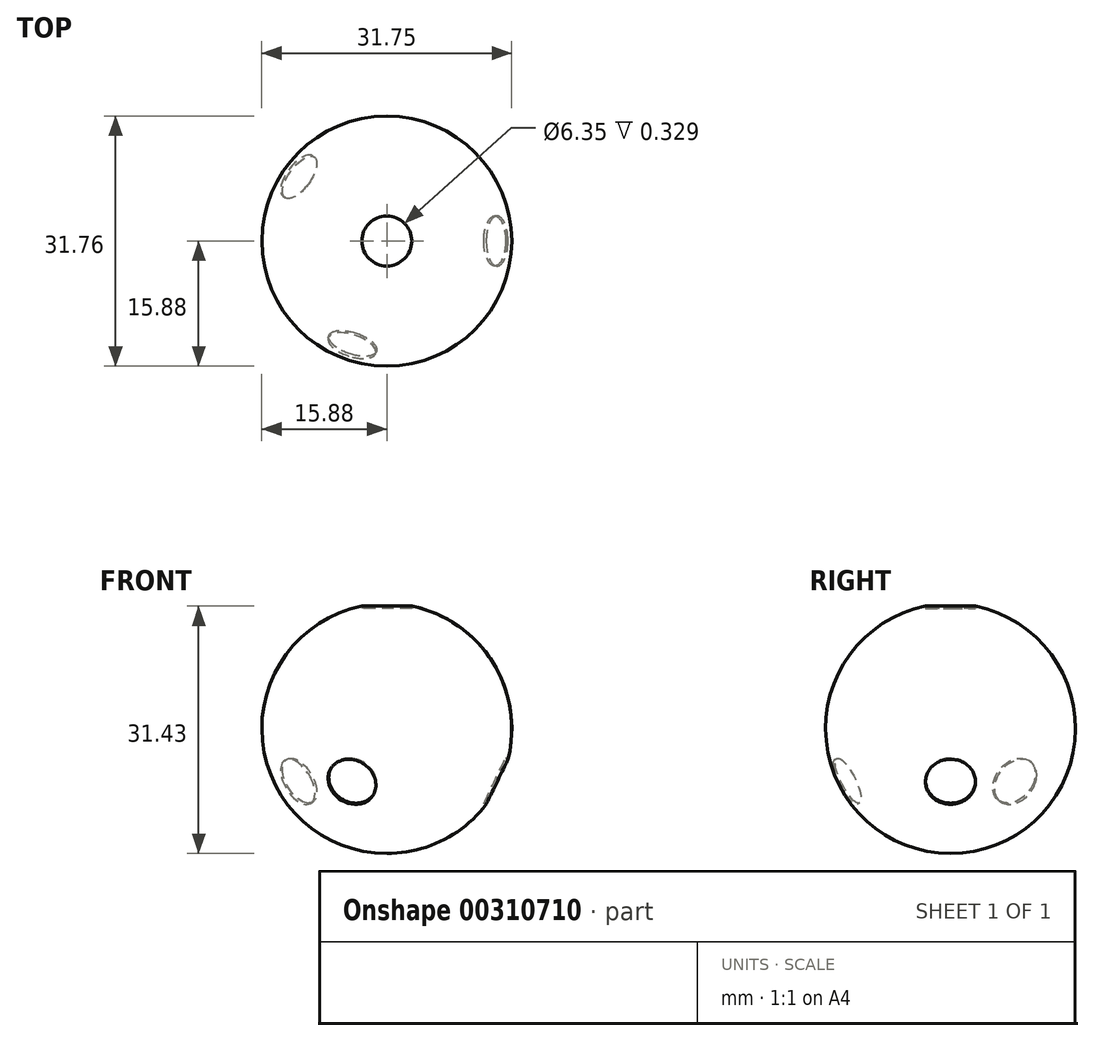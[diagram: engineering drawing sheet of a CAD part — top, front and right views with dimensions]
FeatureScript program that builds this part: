
annotation { "Feature Type Name" : "Feature", "Feature Type Description" : "" }
export const myFeature = defineFeature(function(context is Context, id is Id, definition is map)
    precondition{}
    {
        {
            var Q0;
            Q0=qCreatedBy(makeId("Front.planeOp"),FACE);
            var sketch = newSketch(context, id + "F0", { "sketchPlane" : qUnion([Q0])});
            skArc(sketch, "E0", {"start": v(0, 15.88) * mm, "mid": v(-15.88, 0) * mm, "end": v(0, -15.88) * mm});
            skLineSegment(sketch, "E1", {"start": v(0, 15.88) * mm, "end": v(0, -15.88) * mm});
            skSolve(sketch);
        }
        {
            var Q0;
            Q0=qCreatedBy(makeId("Top.planeOp"),FACE);
            var sketch = newSketch(context, id + "F1", { "sketchPlane" : qUnion([Q0])});
            skCircle(sketch, "E2", {"center": v(0, 0) * mm, "radius": 15.88 * mm});
            skSolve(sketch);
        }
        {
            var Q0;
            Q0=makeQuery(id+"F0.imprint","IMPRINT",FACE,{"disambiguationData":[TD([[makeQuery(id+"F0.imprint","IMPRINT",EDGE,{"derivedFrom":sQuery(id+"F0.wireOp",EDGE,"E0")}),1.0]])]});
            var Q1;
            Q1=sQuery(id+"F1.wireOp",EDGE,"E2");
            revolve(context, id + "F2", {"entities" : qUnion([Q0]), "axis" : qUnion([Q1]), "revolveType" : RevolveType.FULL});
        }
        {
            var Q0;
            Q0=qCreatedBy(makeId("Top.planeOp"),FACE);
            cPlane(context, id + "F3", {"entities" : qUnion([Q0]), "cplaneType" : CPlaneType.OFFSET, "offset" : 15.24 * mm, "width" : 152.4 * mm, "height" : 152.4 * mm});
        }
        {
            var Q0;
            Q0=qCreatedBy(id+"F3.planeOp",FACE);
            cPlane(context, id + "F4", {"entities" : qUnion([Q0]), "cplaneType" : CPlaneType.OFFSET, "offset" : 3 / 203.2 * mm, "oppositeDirection" : true, "width" : 152.4 * mm, "height" : 152.4 * mm});
        }
        {
            var Q0;
            Q0=qCreatedBy(id+"F4.planeOp",FACE);
            var sketch = newSketch(context, id + "F5", { "sketchPlane" : qUnion([Q0])});
            skCircle(sketch, "E3", {"center": v(0, 0) * mm, "radius": 3.18 * mm});
            skSolve(sketch);
        }
        {
            var Q0;
            Q0 = qSketchRegion(id + "F5", true);
            extrude(context, id + "F6", {"entities" : qUnion([Q0]), "depth" : 50.8 * mm});
        }
        {
            var Q0;
            Q0=qCreatedBy(makeId("Front.planeOp"),FACE);
            var sketch = newSketch(context, id + "F7", { "sketchPlane" : qUnion([Q0])});
            skLineSegment(sketch, "E4", {"start": v(0, 0) * mm, "end": v(0, -56.18) * mm, "construction": true});
            skLineSegment(sketch, "E5", {"start": v(0, 0) * mm, "end": v(-70.74, 0) * mm, "construction": true});
            skSolve(sketch);
        }
        {
            var Q0;
            Q0=qCreatedBy(makeId("Right.planeOp"),FACE);
            var sketch = newSketch(context, id + "F8", { "sketchPlane" : qUnion([Q0])});
            skLineSegment(sketch, "E6", {"start": v(0, 0) * mm, "end": v(67.72, 0) * mm, "construction": true});
            skSolve(sketch);
        }
        {
            var Q0;
            Q0=makeQuery(id+"F6.opExtrude","SWEPT_BODY",BODY,{"disambiguationData":[OSD([sQuery(id+"F5.wireOp",EDGE,"E3")])]});
            var Q1;
            Q1=sQuery(id+"F8.wireOp",EDGE,"E6");
            transform(context, id + "F9", {"entities" : qUnion([Q0]), "transformType" : TransformType.ROTATION, "transformAxis" : qUnion([Q1]), "angle" : 115.8 * degree, "makeCopy" : true});
        }
        {
            var Q0;
            Q0=makeQuery(id+"F9.opPattern","COPY",BODY,{"derivedFrom":makeQuery(id+"F6.opExtrude","SWEPT_BODY",BODY,{"disambiguationData":[OSD([sQuery(id+"F5.wireOp",EDGE,"E3")])]}),"instanceName":"1"});
            var Q1;
            Q1=sQuery(id+"F7.wireOp",EDGE,"E4");
            transform(context, id + "F10", {"entities" : qUnion([Q0]), "transformType" : TransformType.ROTATION, "transformAxis" : qUnion([Q1]), "angle" : 108.4 * degree, "makeCopy" : true});
        }
        {
            var Q0;
            Q0=makeQuery(id+"F10.opPattern","COPY",BODY,{"derivedFrom":makeQuery(id+"F9.opPattern","COPY",BODY,{"derivedFrom":makeQuery(id+"F6.opExtrude","SWEPT_BODY",BODY,{"disambiguationData":[OSD([sQuery(id+"F5.wireOp",EDGE,"E3")])]}),"instanceName":"1"}),"instanceName":"1"});
            var Q1;
            Q1=sQuery(id+"F7.wireOp",EDGE,"E4");
            transform(context, id + "F11", {"entities" : qUnion([Q0]), "transformType" : TransformType.ROTATION, "transformAxis" : qUnion([Q1]), "angle" : 107.7 * degree, "makeCopy" : true});
        }
        {
            var Q0;
            Q0=makeQuery(id+"F6.opExtrude","SWEPT_BODY",BODY,{"disambiguationData":[OSD([sQuery(id+"F5.wireOp",EDGE,"E3")])]});
            var Q1;
            Q1=makeQuery(id+"F10.opPattern","COPY",BODY,{"derivedFrom":makeQuery(id+"F9.opPattern","COPY",BODY,{"derivedFrom":makeQuery(id+"F6.opExtrude","SWEPT_BODY",BODY,{"disambiguationData":[OSD([sQuery(id+"F5.wireOp",EDGE,"E3")])]}),"instanceName":"1"}),"instanceName":"1"});
            var Q2;
            Q2=makeQuery(id+"F11.opPattern","COPY",BODY,{"derivedFrom":makeQuery(id+"F10.opPattern","COPY",BODY,{"derivedFrom":makeQuery(id+"F9.opPattern","COPY",BODY,{"derivedFrom":makeQuery(id+"F6.opExtrude","SWEPT_BODY",BODY,{"disambiguationData":[OSD([sQuery(id+"F5.wireOp",EDGE,"E3")])]}),"instanceName":"1"}),"instanceName":"1"}),"instanceName":"1"});
            var Q3;
            Q3=makeQuery(id+"F9.opPattern","COPY",BODY,{"derivedFrom":makeQuery(id+"F6.opExtrude","SWEPT_BODY",BODY,{"disambiguationData":[OSD([sQuery(id+"F5.wireOp",EDGE,"E3")])]}),"instanceName":"1"});
            var Q4;
            Q4=makeQuery(id+"F2.opRevolve","SWEPT_BODY",BODY,{"disambiguationData":[OSD([sQuery(id+"F0.wireOp",EDGE,"E0"),sQuery(id+"F0.wireOp",EDGE,"E1")])]});
            booleanBodies(context, id + "F12", {"operationType" : BooleanOperationType.SUBTRACTION, "tools" : qUnion([Q0, Q1, Q2, Q3]), "targets" : qUnion([Q4])});
        }
    });
